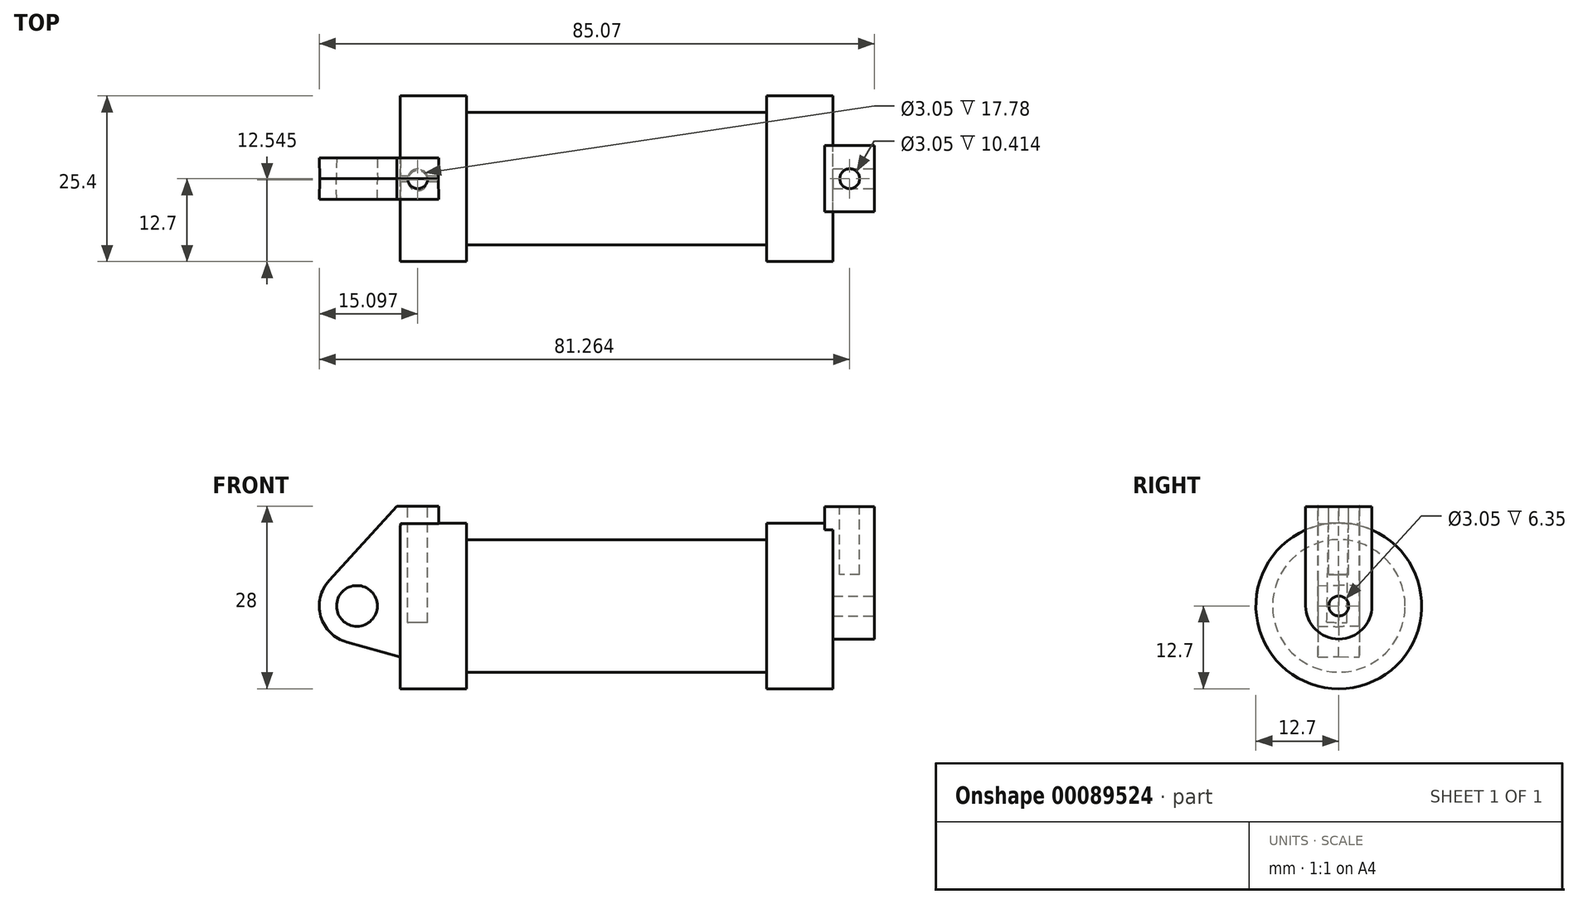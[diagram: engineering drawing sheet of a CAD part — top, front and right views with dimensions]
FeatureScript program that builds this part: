
annotation { "Feature Type Name" : "Feature", "Feature Type Description" : "" }
export const myFeature = defineFeature(function(context is Context, id is Id, definition is map)
    precondition{}
    {
        {
            var Q0;
            Q0=qCreatedBy(makeId("Front.planeOp"),FACE);
            var sketch = newSketch(context, id + "F0", { "sketchPlane" : qUnion([Q0])});
            skLineSegment(sketch, "E0", {"start": v(0, 0) * mm, "end": v(0, 12.7) * mm});
            skLineSegment(sketch, "E1", {"start": v(0, 12.7) * mm, "end": v(10.16, 12.7) * mm});
            skLineSegment(sketch, "E2", {"start": v(10.16, 12.7) * mm, "end": v(10.16, 10.16) * mm});
            skLineSegment(sketch, "E3", {"start": v(10.16, 10.16) * mm, "end": v(56.13, 10.16) * mm});
            skLineSegment(sketch, "E4", {"start": v(56.13, 10.16) * mm, "end": v(56.13, 12.7) * mm});
            skLineSegment(sketch, "E5", {"start": v(56.13, 12.7) * mm, "end": v(66.3, 12.7) * mm});
            skLineSegment(sketch, "E6", {"start": v(66.3, 12.7) * mm, "end": v(66.3, 0) * mm});
            skLineSegment(sketch, "E7", {"start": v(66.3, 0) * mm, "end": v(0, 0) * mm});
            skLineSegment(sketch, "E8", {"start": v(5.84, 15.24) * mm, "end": v(-0.5, 15.24) * mm});
            skLineSegment(sketch, "E9", {"start": v(-0.5, 15.24) * mm, "end": v(-10.88, 3.85) * mm});
            skLineSegment(sketch, "E10", {"start": v(0, 0) * mm, "end": v(-6.65, 0) * mm});
            skCircle(sketch, "E11", {"center": v(-6.65, 0) * mm, "radius": 5.72 * mm});
            skCircle(sketch, "E12", {"center": v(-6.65, 0) * mm, "radius": 3.18 * mm});
            skLineSegment(sketch, "E13", {"start": v(5.84, 15.24) * mm, "end": v(5.84, -9.4) * mm});
            skLineSegment(sketch, "E14", {"start": v(5.84, -9.4) * mm, "end": v(-8.18, -5.5) * mm});
            skSolve(sketch);
        }
        {
            var Q0;
            {var subQ0=sQuery(id+"F0.wireOp",EDGE,"E2");Q0=makeQuery(id+"F0.imprint","IMPRINT",FACE,{"disambiguationData":[TD([[makeQuery(id+"F0.imprint","IMPRINT",EDGE,{"derivedFrom":subQ0}),-1.0]])]});}
            var Q1;
            {var subQ0=sQuery(id+"F0.wireOp",EDGE,"E0");Q1=makeQuery(id+"F0.imprint","IMPRINT",FACE,{"disambiguationData":[TD([[makeQuery(id+"F0.imprint","IMPRINT",EDGE,{"derivedFrom":subQ0}),-1.0]])]});}
            var Q2;
            Q2=sQuery(id+"F0.wireOp",EDGE,"E7");
            revolve(context, id + "F1", {"entities" : qUnion([Q0, Q1]), "axis" : qUnion([Q2]), "revolveType" : RevolveType.FULL});
        }
        {
            var Q0;
            {var subQ0=sQuery(id+"F0.wireOp",EDGE,"E14");Q0=makeQuery(id+"F0.imprint","IMPRINT",FACE,{"disambiguationData":[TD([[makeQuery(id+"F0.imprint","IMPRINT",EDGE,{"derivedFrom":subQ0}),-1.0]])]});}
            var Q1;
            {var subQ4=sQuery(id+"F0.wireOp",EDGE,"E12");Q1=makeQuery(id+"F0.imprint","IMPRINT",FACE,{"disambiguationData":[TD([[makeQuery(id+"F0.imprint","IMPRINT",EDGE,{"derivedFrom":subQ4}),-1.0]])]});}
            var Q2;
            {var subQ3=sQuery(id+"F0.wireOp",EDGE,"E0");Q2=makeQuery(id+"F0.imprint","IMPRINT",FACE,{"disambiguationData":[TD([[makeQuery(id+"F0.imprint","IMPRINT",EDGE,{"derivedFrom":subQ3}),1.0]])]});}
            extrude(context, id + "F2", {"entities" : qUnion([Q0, Q1, Q2]), "operationType" : NewBodyOperationType.ADD, "endBound" : BoundingType.SYMMETRIC, "depth" : 6.35 * mm, "hasDraft" : true, "draftAngle" : 1 * degree});
        }
        {
            var Q0;
            Q0=makeQuery(id+"F1.opRevolve","SWEPT_FACE",FACE,{"disambiguationData":[OSD([sQuery(id+"F0.wireOp",EDGE,"E6")])]});
            var sketch = newSketch(context, id + "F3", { "sketchPlane" : qUnion([Q0])});
            skCircle(sketch, "E15", {"center": v(0, 0) * mm, "radius": 5.08 * mm});
            skCircle(sketch, "E16", {"center": v(0, 0) * mm, "radius": 1.52 * mm});
            skLineSegment(sketch, "E17", {"start": v(0, 0) * mm, "end": v(12.7, 0) * mm, "construction": true});
            skLineSegment(sketch, "E18", {"start": v(0, 0) * mm, "end": v(-12.7, 0) * mm, "construction": true});
            skLineSegment(sketch, "E19", {"start": v(-5.08, 0) * mm, "end": v(-5.08, 15.24) * mm});
            skLineSegment(sketch, "E20", {"start": v(5.08, 0) * mm, "end": v(5.08, 15.24) * mm});
            skLineSegment(sketch, "E21", {"start": v(-5.08, 15.24) * mm, "end": v(5.08, 15.24) * mm});
            skSolve(sketch);
        }
        {
            var Q0;
            {var subQ0=sQuery(id+"F3.wireOp",EDGE,"E21");Q0=makeQuery(id+"F3.imprint","IMPRINT",FACE,{"disambiguationData":[TD([[makeQuery(id+"F3.imprint","IMPRINT",EDGE,{"derivedFrom":subQ0}),-1.0]])]});}
            extrude(context, id + "F4", {"entities" : qUnion([Q0]), "operationType" : NewBodyOperationType.ADD, "oppositeDirection" : true, "depth" : 1.27 * mm});
        }
        {
            var Q0;
            {var subQ0=sQuery(id+"F3.wireOp",EDGE,"E21");Q0=makeQuery(id+"F3.imprint","IMPRINT",FACE,{"disambiguationData":[TD([[makeQuery(id+"F3.imprint","IMPRINT",EDGE,{"derivedFrom":subQ0}),-1.0]])]});}
            var Q1;
            {var subQ0=sQuery(id+"F3.wireOp",EDGE,"E19");var subQ1=sQuery(id+"F3.wireOp",EDGE,"E15");var subQ2=makeQuery(id+"F3.imprint","INTERSECT",VERTEX,{"derivedFrom":[subQ1,subQ0]});Q1=makeQuery(id+"F3.imprint","IMPRINT",FACE,{"disambiguationData":[TD([[makeQuery(id+"F3.imprint","IMPRINT",EDGE,{"disambiguationData":[TD([[subQ2,1.0]])],"derivedFrom":subQ1}),-1.0]])]});}
            var Q2;
            Q2=makeQuery(id+"F3.imprint","IMPRINT",FACE,{"disambiguationData":[TD([[makeQuery(id+"F3.imprint","IMPRINT",EDGE,{"derivedFrom":sQuery(id+"F3.wireOp",EDGE,"E16")}),-1.0]])]});
            var Q3;
            Q3=makeQuery(id+"F3.imprint","IMPRINT",FACE,{"disambiguationData":[TD([[makeQuery(id+"F3.imprint","IMPRINT",EDGE,{"derivedFrom":sQuery(id+"F3.wireOp",EDGE,"E16")}),1.0]])]});
            extrude(context, id + "F5", {"entities" : qUnion([Q0, Q1, Q2, Q3]), "operationType" : NewBodyOperationType.ADD, "depth" : 6.35 * mm});
        }
        {
            var Q0;
            Q0=makeQuery(id+"F5.opExtrude","CAP_FACE",FACE,{"disambiguationData":[OSD([sQuery(id+"F3.wireOp",EDGE,"E15"),sQuery(id+"F3.wireOp",EDGE,"E19"),sQuery(id+"F3.wireOp",EDGE,"E20"),sQuery(id+"F3.wireOp",EDGE,"E21")])],"isStart":false});
            var sketch = newSketch(context, id + "F6", { "sketchPlane" : qUnion([Q0])});
            skCircle(sketch, "E22", {"center": v(0, 0) * mm, "radius": 1.52 * mm});
            skSolve(sketch);
        }
        {
            var Q0;
            Q0=makeQuery(id+"F6.imprint","IMPRINT",FACE,{"disambiguationData":[TD([[makeQuery(id+"F6.imprint","IMPRINT",EDGE,{"derivedFrom":sQuery(id+"F6.wireOp",EDGE,"E22")}),1.0]])]});
            var Q1;
            Q1=sQuery(id+"F6.wireOp",EDGE,"E22");
            var Q2;
            {var subQ0=sQuery(id+"F0.wireOp",EDGE,"E6");Q2=makeQuery(id+"F4.boolean.opBoolean","MERGE",FACE,{"derivedFrom":[makeQuery(id+"F1.opRevolve","SWEPT_FACE",FACE,{"disambiguationData":[OSD([subQ0])]}),makeQuery(id+"F4.opExtrude","CAP_FACE",FACE,{"disambiguationData":[OSD([sQuery(id+"F0.wireOp",EDGE,"E5"),subQ0,sQuery(id+"F3.wireOp",EDGE,"E19"),sQuery(id+"F3.wireOp",EDGE,"E20"),sQuery(id+"F3.wireOp",EDGE,"E21")])],"isStart":true})]});}
            extrude(context, id + "F7", {"entities" : qUnion([Q0]), "operationType" : NewBodyOperationType.REMOVE, "surfaceEntities" : qUnion([Q1]), "endBound" : BoundingType.UP_TO_SURFACE, "oppositeDirection" : true, "endBoundEntityFace" : qUnion([Q2]), "depth" : 25.4 * mm});
        }
        {
            var Q0;
            Q0=makeQuery(id+"F2.opExtrude","SWEPT_FACE",FACE,{"disambiguationData":[OSD([sQuery(id+"F0.wireOp",EDGE,"E8")])]});
            var sketch = newSketch(context, id + "F8", { "sketchPlane" : qUnion([Q0])});
            skCircle(sketch, "E23", {"center": v(2.67, -0.27) * mm, "radius": 1.52 * mm});
            skSolve(sketch);
        }
        {
            var Q0;
            Q0 = qSketchRegion(id + "F8", true);
            extrude(context, id + "F9", {"entities" : qUnion([Q0]), "operationType" : NewBodyOperationType.REMOVE, "oppositeDirection" : true, "depth" : 17.78 * mm});
        }
        {
            var Q0;
            {var subQ0=sQuery(id+"F3.wireOp",EDGE,"E21");Q0=makeQuery(id+"F5.boolean.opBoolean","MERGE",FACE,{"derivedFrom":[makeQuery(id+"F4.opExtrude","SWEPT_FACE",FACE,{"disambiguationData":[OSD([subQ0])]}),makeQuery(id+"F5.opExtrude","SWEPT_FACE",FACE,{"disambiguationData":[OSD([subQ0])]})]});}
            var sketch = newSketch(context, id + "F10", { "sketchPlane" : qUnion([Q0])});
            skLineSegment(sketch, "E24", {"start": v(68.83, 5.08) * mm, "end": v(68.83, -5.08) * mm, "construction": true});
            skCircle(sketch, "E25", {"center": v(68.83, 0) * mm, "radius": 1.52 * mm});
            skSolve(sketch);
        }
        {
            var Q0;
            Q0=makeQuery(id+"F10.imprint","IMPRINT",FACE,{"disambiguationData":[TD([[makeQuery(id+"F10.imprint","IMPRINT",EDGE,{"derivedFrom":sQuery(id+"F10.wireOp",EDGE,"E25")}),1.0]])]});
            var Q1;
            Q1=sQuery(id+"F10.wireOp",EDGE,"E25");
            extrude(context, id + "F11", {"entities" : qUnion([Q0]), "operationType" : NewBodyOperationType.REMOVE, "surfaceEntities" : qUnion([Q1]), "oppositeDirection" : true, "depth" : 10.4 * mm});
        }
    });
